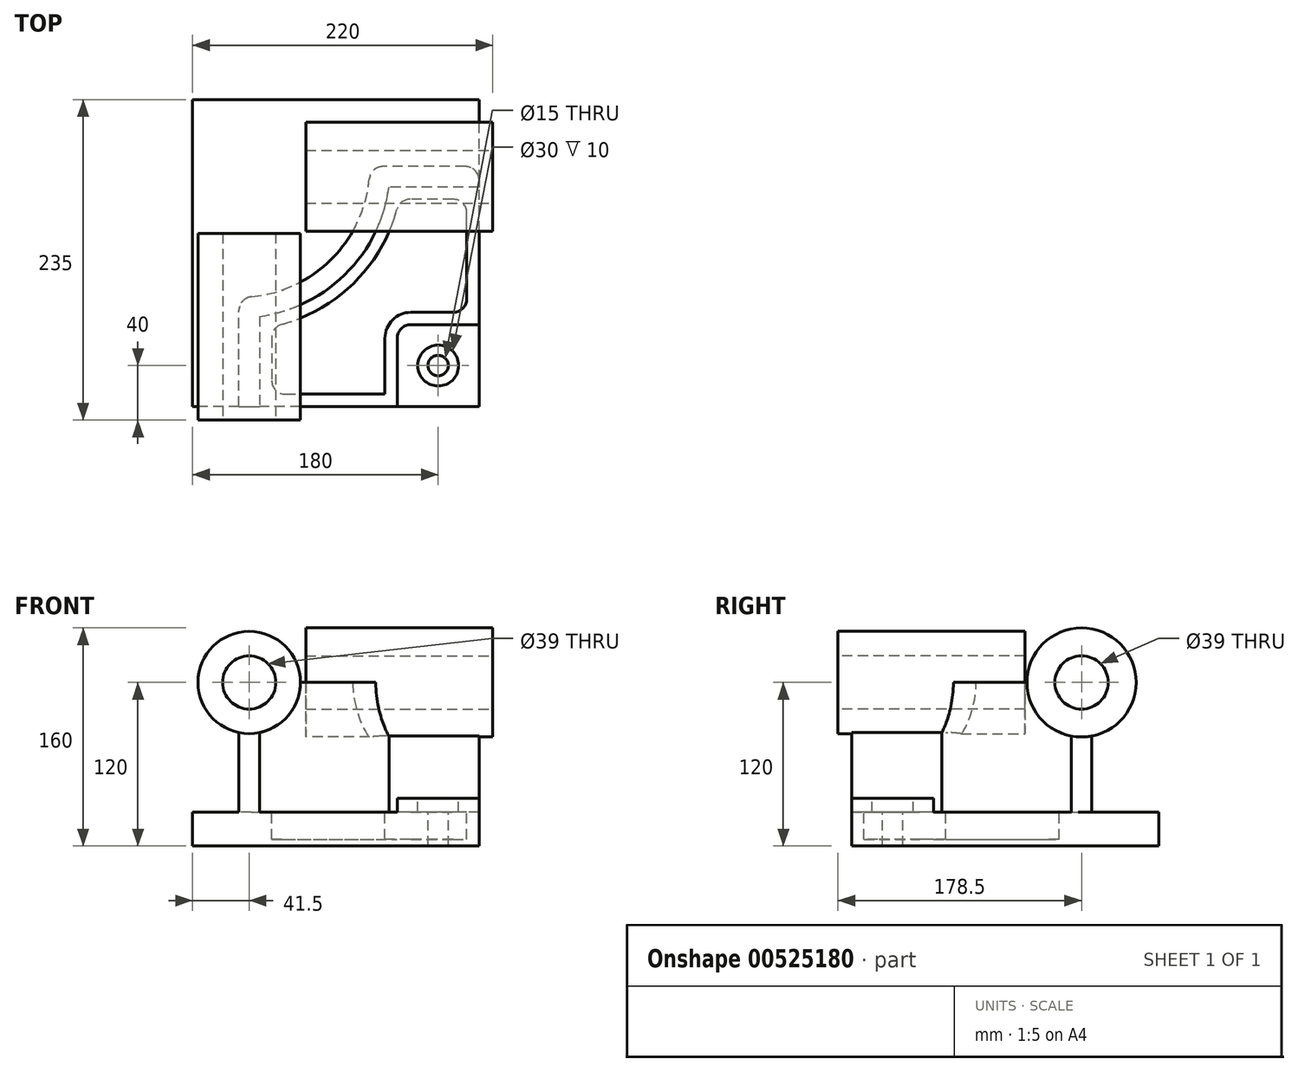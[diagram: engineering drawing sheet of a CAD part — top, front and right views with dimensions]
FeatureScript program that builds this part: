
annotation { "Feature Type Name" : "Feature", "Feature Type Description" : "" }
export const myFeature = defineFeature(function(context is Context, id is Id, definition is map)
    precondition{}
    {
        {
            var Q0;
            Q0=qCreatedBy(makeId("Top.planeOp"),FACE);
            var sketch = newSketch(context, id + "F0", { "sketchPlane" : qUnion([Q0])});
            skLineSegment(sketch, "E0.bottom", {"start": v(105, -112.5) * mm, "end": v(-105, -112.5) * mm});
            skLineSegment(sketch, "E0.top", {"start": v(105, 112.5) * mm, "end": v(-105, 112.5) * mm});
            skLineSegment(sketch, "E0.left", {"start": v(105, -112.5) * mm, "end": v(105, 112.5) * mm});
            skLineSegment(sketch, "E0.right", {"start": v(-105, -112.5) * mm, "end": v(-105, 112.5) * mm});
            skPoint(sketch, "E0.middle", {"position": v(0, 0) * mm});
            skSolve(sketch);
        }
        {
            var Q0;
            Q0=makeQuery(id+"F0.imprint","IMPRINT",FACE,{"disambiguationData":[TD([[makeQuery(id+"F0.imprint","IMPRINT",EDGE,{"derivedFrom":sQuery(id+"F0.wireOp",EDGE,"E0.bottom")}),-1.0]])]});
            extrude(context, id + "F1", {"entities" : qUnion([Q0]), "depth" : 25 * mm, "offsetDistance" : 25 * mm});
        }
        {
            var Q0;
            Q0=makeQuery(id+"F1.opExtrude","CAP_FACE",FACE,{"disambiguationData":[OSD([sQuery(id+"F0.wireOp",EDGE,"E0.bottom"),sQuery(id+"F0.wireOp",EDGE,"E0.top"),sQuery(id+"F0.wireOp",EDGE,"E0.left"),sQuery(id+"F0.wireOp",EDGE,"E0.right")])],"isStart":false});
            var sketch = newSketch(context, id + "F2", { "sketchPlane" : qUnion([Q0])});
            skLineSegment(sketch, "E1", {"start": v(105, 63.5) * mm, "end": v(25, 63.5) * mm});
            skArc(sketch, "E2", {"start": v(-71, -32.5) * mm, "mid": v(-3.12, -4.38) * mm, "end": v(25, 63.5) * mm});
            skLineSegment(sketch, "E3", {"start": v(-71, -32.5) * mm, "end": v(-71, -112.5) * mm});
            skLineSegment(sketch, "E4", {"start": v(-71, -32.5) * mm, "end": v(-71, 87.2) * mm, "construction": true});
            skLineSegment(sketch, "E5", {"start": v(25, 63.5) * mm, "end": v(-95.53, 63.5) * mm, "construction": true});
            skLineSegment(sketch, "E6.0", {"start": v(-56, -46.48) * mm, "end": v(-56, -112.5) * mm});
            skArc(sketch, "E6.1", {"start": v(-56, -46.48) * mm, "mid": v(7.49, -14.99) * mm, "end": v(38.98, 48.5) * mm});
            skLineSegment(sketch, "E6.2", {"start": v(105, 48.5) * mm, "end": v(38.98, 48.5) * mm});
            skLineSegment(sketch, "E7.0", {"start": v(105, -112.5) * mm, "end": v(105, 112.5) * mm});
            skLineSegment(sketch, "E8.0", {"start": v(105, -112.5) * mm, "end": v(-105, -112.5) * mm});
            skSolve(sketch);
        }
        {
            var Q0;
            {var subQ2=sQuery(id+"F2.wireOp",EDGE,"E1");Q0=makeQuery(id+"F2.imprint","IMPRINT",FACE,{"disambiguationData":[TD([[makeQuery(id+"F2.imprint","IMPRINT",EDGE,{"derivedFrom":subQ2}),1.0]])]});}
            extrude(context, id + "F3", {"entities" : qUnion([Q0]), "operationType" : NewBodyOperationType.ADD, "depth" : 95 * mm, "offsetDistance" : 25 * mm});
        }
        {
            var Q0;
            Q0=makeQuery(id+"F3.boolean.opBoolean","MERGE",FACE,{"derivedFrom":[makeQuery(id+"F1.opExtrude","SWEPT_FACE",FACE,{"disambiguationData":[OSD([sQuery(id+"F0.wireOp",EDGE,"E0.bottom")])]}),makeQuery(id+"F3.opExtrude","SWEPT_FACE",FACE,{"disambiguationData":[OSD([sQuery(id+"F2.wireOp",EDGE,"E8.0")])]})]});
            var sketch = newSketch(context, id + "F4", { "sketchPlane" : qUnion([Q0])});
            skCircle(sketch, "E9", {"center": v(-63.5, 120) * mm, "radius": 37.5 * mm});
            skSolve(sketch);
        }
        {
            var Q0;
            {var subQ1=sQuery(id+"F2.wireOp",EDGE,"E8.0");var subQ6=makeQuery(id+"F3.opExtrude","CAP_EDGE",EDGE,{"disambiguationData":[OSD([subQ1])],"isStart":false});Q0=makeQuery(id+"F4.imprint","IMPRINT",FACE,{"disambiguationData":[TD([[makeQuery(id+"F4.imprint","IMPRINT",EDGE,{"derivedFrom":subQ6}),-1.0]])]});}
            var Q1;
            {var subQ1=sQuery(id+"F2.wireOp",EDGE,"E8.0");var subQ6=makeQuery(id+"F3.opExtrude","CAP_EDGE",EDGE,{"disambiguationData":[OSD([subQ1])],"isStart":false});Q1=makeQuery(id+"F4.imprint","IMPRINT",FACE,{"disambiguationData":[TD([[makeQuery(id+"F4.imprint","IMPRINT",EDGE,{"derivedFrom":subQ6}),1.0]])]});}
            extrude(context, id + "F5", {"entities" : qUnion([Q0, Q1]), "operationType" : NewBodyOperationType.ADD, "depth" : 10 * mm, "offsetDistance" : 25 * mm, "hasSecondDirection" : true, "secondDirectionOppositeDirection" : true, "secondDirectionDepth" : 127 * mm});
        }
        {
            var Q0;
            Q0=makeQuery(id+"F3.boolean.opBoolean","MERGE",FACE,{"derivedFrom":[makeQuery(id+"F1.opExtrude","SWEPT_FACE",FACE,{"disambiguationData":[OSD([sQuery(id+"F0.wireOp",EDGE,"E0.left")])]}),makeQuery(id+"F3.opExtrude","SWEPT_FACE",FACE,{"disambiguationData":[OSD([sQuery(id+"F2.wireOp",EDGE,"E7.0")])]})]});
            var sketch = newSketch(context, id + "F6", { "sketchPlane" : qUnion([Q0])});
            skCircle(sketch, "E10", {"center": v(56, 120) * mm, "radius": 40 * mm});
            skSolve(sketch);
        }
        {
            var Q0;
            {var subQ1=sQuery(id+"F2.wireOp",EDGE,"E7.0");var subQ6=makeQuery(id+"F3.opExtrude","CAP_EDGE",EDGE,{"disambiguationData":[OSD([subQ1])],"isStart":false});Q0=makeQuery(id+"F6.imprint","IMPRINT",FACE,{"disambiguationData":[TD([[makeQuery(id+"F6.imprint","IMPRINT",EDGE,{"derivedFrom":subQ6}),-1.0]])]});}
            var Q1;
            {var subQ1=sQuery(id+"F2.wireOp",EDGE,"E7.0");var subQ6=makeQuery(id+"F3.opExtrude","CAP_EDGE",EDGE,{"disambiguationData":[OSD([subQ1])],"isStart":false});Q1=makeQuery(id+"F6.imprint","IMPRINT",FACE,{"disambiguationData":[TD([[makeQuery(id+"F6.imprint","IMPRINT",EDGE,{"derivedFrom":subQ6}),1.0]])]});}
            extrude(context, id + "F7", {"entities" : qUnion([Q0, Q1]), "operationType" : NewBodyOperationType.ADD, "depth" : 10 * mm, "offsetDistance" : 25 * mm, "hasSecondDirection" : true, "secondDirectionOppositeDirection" : true, "secondDirectionDepth" : 127 * mm});
        }
        {
            var Q0;
            {var subQ0=sQuery(id+"F0.wireOp",EDGE,"E0.left");var subQ1=sQuery(id+"F0.wireOp",EDGE,"E0.bottom");Q0=makeQuery(id+"F3.boolean.opBoolean","SPLIT",FACE,{"disambiguationData":[TD([makeQuery(id+"F3.opExtrude","SWEPT_FACE",FACE,{"disambiguationData":[OSD([sQuery(id+"F2.wireOp",EDGE,"E6.0")])]})])],"derivedFrom":makeQuery(id+"F1.opExtrude","CAP_FACE",FACE,{"disambiguationData":[OSD([subQ1,sQuery(id+"F0.wireOp",EDGE,"E0.top"),subQ0,sQuery(id+"F0.wireOp",EDGE,"E0.right")])],"isStart":false})});}
            var sketch = newSketch(context, id + "F8", { "sketchPlane" : qUnion([Q0])});
            skLineSegment(sketch, "E11.bottom", {"start": v(105, -112.5) * mm, "end": v(45, -112.5) * mm});
            skLineSegment(sketch, "E11.top", {"start": v(105, -52.5) * mm, "end": v(45, -52.5) * mm});
            skLineSegment(sketch, "E11.left", {"start": v(105, -112.5) * mm, "end": v(105, -52.5) * mm});
            skLineSegment(sketch, "E11.right", {"start": v(45, -112.5) * mm, "end": v(45, -52.5) * mm});
            skSolve(sketch);
        }
        {
            var Q0;
            Q0=makeQuery(id+"F8.imprint","IMPRINT",FACE,{"disambiguationData":[TD([[makeQuery(id+"F8.imprint","IMPRINT",EDGE,{"derivedFrom":sQuery(id+"F8.wireOp",EDGE,"E11.bottom")}),-1.0]])]});
            extrude(context, id + "F9", {"entities" : qUnion([Q0]), "operationType" : NewBodyOperationType.ADD, "depth" : 10 * mm, "offsetDistance" : 25 * mm});
        }
        {
            var Q0;
            Q0=makeQuery(id+"F9.opExtrude","SWEPT_EDGE",EDGE,{"disambiguationData":[OSD([sQuery(id+"F8.wireOp",EDGE,"E11.top"),sQuery(id+"F8.wireOp",EDGE,"E11.right")])]});
            fillet(context, id + "F10", {"entities" : qUnion([Q0]), "radius" : 10 * mm, "tangentPropagation" : true, "allowEdgeOverflow" : false});
        }
        {
            var Q0;
            {var subQ0=sQuery(id+"F0.wireOp",EDGE,"E0.left");var subQ1=sQuery(id+"F0.wireOp",EDGE,"E0.bottom");Q0=makeQuery(id+"F3.boolean.opBoolean","SPLIT",FACE,{"disambiguationData":[TD([makeQuery(id+"F3.opExtrude","SWEPT_FACE",FACE,{"disambiguationData":[OSD([sQuery(id+"F2.wireOp",EDGE,"E6.0")])]})])],"derivedFrom":makeQuery(id+"F1.opExtrude","CAP_FACE",FACE,{"disambiguationData":[OSD([subQ1,sQuery(id+"F0.wireOp",EDGE,"E0.top"),subQ0,sQuery(id+"F0.wireOp",EDGE,"E0.right")])],"isStart":false})});}
            var sketch = newSketch(context, id + "F11", { "sketchPlane" : qUnion([Q0])});
            skLineSegment(sketch, "E12.0", {"start": v(-47, -54.08) * mm, "end": v(-47, -103.5) * mm});
            skArc(sketch, "E12.1", {"start": v(46.58, 39.5) * mm, "mid": v(13.85, -21.35) * mm, "end": v(-47, -54.08) * mm});
            skLineSegment(sketch, "E12.2", {"start": v(-47, -103.5) * mm, "end": v(36, -103.5) * mm});
            skLineSegment(sketch, "E12.3", {"start": v(96, 39.5) * mm, "end": v(46.58, 39.5) * mm});
            skLineSegment(sketch, "E12.4", {"start": v(36, -103.5) * mm, "end": v(36, -62.5) * mm});
            skArc(sketch, "E12.5", {"start": v(36, -62.5) * mm, "mid": v(41.56, -49.06) * mm, "end": v(55, -43.5) * mm});
            skLineSegment(sketch, "E12.6", {"start": v(55, -43.5) * mm, "end": v(96, -43.5) * mm});
            skLineSegment(sketch, "E12.7", {"start": v(96, -43.5) * mm, "end": v(96, 39.5) * mm});
            skSolve(sketch);
        }
        {
            var Q0;
            Q0=makeQuery(id+"F11.imprint","IMPRINT",FACE,{"disambiguationData":[TD([[makeQuery(id+"F11.imprint","IMPRINT",EDGE,{"derivedFrom":sQuery(id+"F11.wireOp",EDGE,"E12.0")}),1.0]])]});
            extrude(context, id + "F12", {"entities" : qUnion([Q0]), "operationType" : NewBodyOperationType.REMOVE, "oppositeDirection" : true, "depth" : 20 * mm, "offsetDistance" : 25 * mm});
        }
        {
            var Q0;
            Q0=makeQuery(id+"F9.opExtrude","CAP_FACE",FACE,{"disambiguationData":[OSD([sQuery(id+"F8.wireOp",EDGE,"E11.bottom"),sQuery(id+"F8.wireOp",EDGE,"E11.top"),sQuery(id+"F8.wireOp",EDGE,"E11.left"),sQuery(id+"F8.wireOp",EDGE,"E11.right")])],"isStart":false});
            var sketch = newSketch(context, id + "F13", { "sketchPlane" : qUnion([Q0])});
            skCircle(sketch, "E13", {"center": v(75, -82.5) * mm, "radius": 15 * mm});
            skPoint(sketch, "E14", {"position": v(75, -112.5) * mm});
            skPoint(sketch, "E15", {"position": v(105, -82.5) * mm});
            skSolve(sketch);
        }
        {
            var Q0;
            Q0=sQuery(id+"F13.wireOp",VERTEX,"E13.center");
            var Q1;
            Q1=makeQuery(id+"F1.opExtrude","SWEPT_BODY",BODY,{"disambiguationData":[OSD([sQuery(id+"F0.wireOp",EDGE,"E0.bottom"),sQuery(id+"F0.wireOp",EDGE,"E0.top"),sQuery(id+"F0.wireOp",EDGE,"E0.left"),sQuery(id+"F0.wireOp",EDGE,"E0.right")])]});
            hole(context, id + "F14", {"style" : HoleStyle.C_BORE, "endStyle" : HoleEndStyle.THROUGH, "holeDiameter" : 15 * mm, "cBoreDiameter" : 30 * mm, "cBoreDepth" : 10 * mm, "isTappedThrough" : true, "tappedDepth" : 12 * mm, "tapClearance" : 3, "locations" : qUnion([Q0]), "scope" : qUnion([Q1])});
        }
        {
            var Q0;
            Q0=makeQuery(id+"F12.boolean.opBoolean","COPY",EDGE,{"derivedFrom":makeQuery(id+"F12.opExtrude","SWEPT_EDGE",EDGE,{"disambiguationData":[OSD([sQuery(id+"F11.wireOp",EDGE,"E12.0"),sQuery(id+"F11.wireOp",EDGE,"E12.1")])]})});
            var Q1;
            Q1=makeQuery(id+"F12.boolean.opBoolean","COPY",EDGE,{"derivedFrom":makeQuery(id+"F12.opExtrude","SWEPT_EDGE",EDGE,{"disambiguationData":[OSD([sQuery(id+"F11.wireOp",EDGE,"E12.1"),sQuery(id+"F11.wireOp",EDGE,"E12.3")])]})});
            var Q2;
            Q2=makeQuery(id+"F12.boolean.opBoolean","COPY",EDGE,{"derivedFrom":makeQuery(id+"F12.opExtrude","SWEPT_EDGE",EDGE,{"disambiguationData":[OSD([sQuery(id+"F11.wireOp",EDGE,"E12.3"),sQuery(id+"F11.wireOp",EDGE,"E12.7")])]})});
            var Q3;
            Q3=makeQuery(id+"F12.boolean.opBoolean","COPY",EDGE,{"derivedFrom":makeQuery(id+"F12.opExtrude","SWEPT_EDGE",EDGE,{"disambiguationData":[OSD([sQuery(id+"F11.wireOp",EDGE,"E12.6"),sQuery(id+"F11.wireOp",EDGE,"E12.7")])]})});
            var Q4;
            Q4=makeQuery(id+"F12.boolean.opBoolean","COPY",EDGE,{"derivedFrom":makeQuery(id+"F12.opExtrude","SWEPT_EDGE",EDGE,{"disambiguationData":[OSD([sQuery(id+"F11.wireOp",EDGE,"E12.0"),sQuery(id+"F11.wireOp",EDGE,"E12.2")])]})});
            var Q5;
            Q5=makeQuery(id+"F3.opExtrude","SWEPT_EDGE",EDGE,{"disambiguationData":[OSD([sQuery(id+"F2.wireOp",EDGE,"E1"),sQuery(id+"F2.wireOp",EDGE,"E7.0")])]});
            var Q6;
            Q6=makeQuery(id+"F3.opExtrude","SWEPT_EDGE",EDGE,{"disambiguationData":[OSD([sQuery(id+"F2.wireOp",EDGE,"E1"),sQuery(id+"F2.wireOp",EDGE,"E2")])]});
            var Q7;
            Q7=makeQuery(id+"F3.opExtrude","SWEPT_EDGE",EDGE,{"disambiguationData":[OSD([sQuery(id+"F2.wireOp",EDGE,"E2"),sQuery(id+"F2.wireOp",EDGE,"E3")])]});
            fillet(context, id + "F15", {"entities" : qUnion([Q0, Q1, Q2, Q3, Q4, Q5, Q6, Q7]), "radius" : 10 * mm, "tangentPropagation" : true, "allowEdgeOverflow" : false});
        }
        {
            var Q0;
            Q0=makeQuery(id+"F5.opExtrude","CAP_FACE",FACE,{"disambiguationData":[OSD([sQuery(id+"F4.wireOp",EDGE,"E9")])],"isStart":false});
            var sketch = newSketch(context, id + "F16", { "sketchPlane" : qUnion([Q0])});
            skCircle(sketch, "E16", {"center": v(-63.5, 120) * mm, "radius": 19.5 * mm});
            skSolve(sketch);
        }
        {
            var Q0;
            Q0=makeQuery(id+"F16.imprint","IMPRINT",FACE,{"disambiguationData":[TD([[makeQuery(id+"F16.imprint","IMPRINT",EDGE,{"derivedFrom":sQuery(id+"F16.wireOp",EDGE,"E16")}),1.0]])]});
            extrude(context, id + "F17", {"entities" : qUnion([Q0]), "operationType" : NewBodyOperationType.REMOVE, "endBound" : BoundingType.THROUGH_ALL, "oppositeDirection" : true, "depth" : 25 * mm, "offsetDistance" : 25 * mm});
        }
        {
            var Q0;
            Q0=makeQuery(id+"F7.opExtrude","CAP_FACE",FACE,{"disambiguationData":[OSD([sQuery(id+"F6.wireOp",EDGE,"E10")])],"isStart":false});
            var sketch = newSketch(context, id + "F18", { "sketchPlane" : qUnion([Q0])});
            skCircle(sketch, "E17", {"center": v(56, 120) * mm, "radius": 19.5 * mm});
            skSolve(sketch);
        }
        {
            var Q0;
            Q0=makeQuery(id+"F18.imprint","IMPRINT",FACE,{"disambiguationData":[TD([[makeQuery(id+"F18.imprint","IMPRINT",EDGE,{"derivedFrom":sQuery(id+"F18.wireOp",EDGE,"E17")}),1.0]])]});
            extrude(context, id + "F19", {"entities" : qUnion([Q0]), "operationType" : NewBodyOperationType.REMOVE, "endBound" : BoundingType.THROUGH_ALL, "oppositeDirection" : true, "depth" : 25 * mm, "offsetDistance" : 25 * mm});
        }
    });
